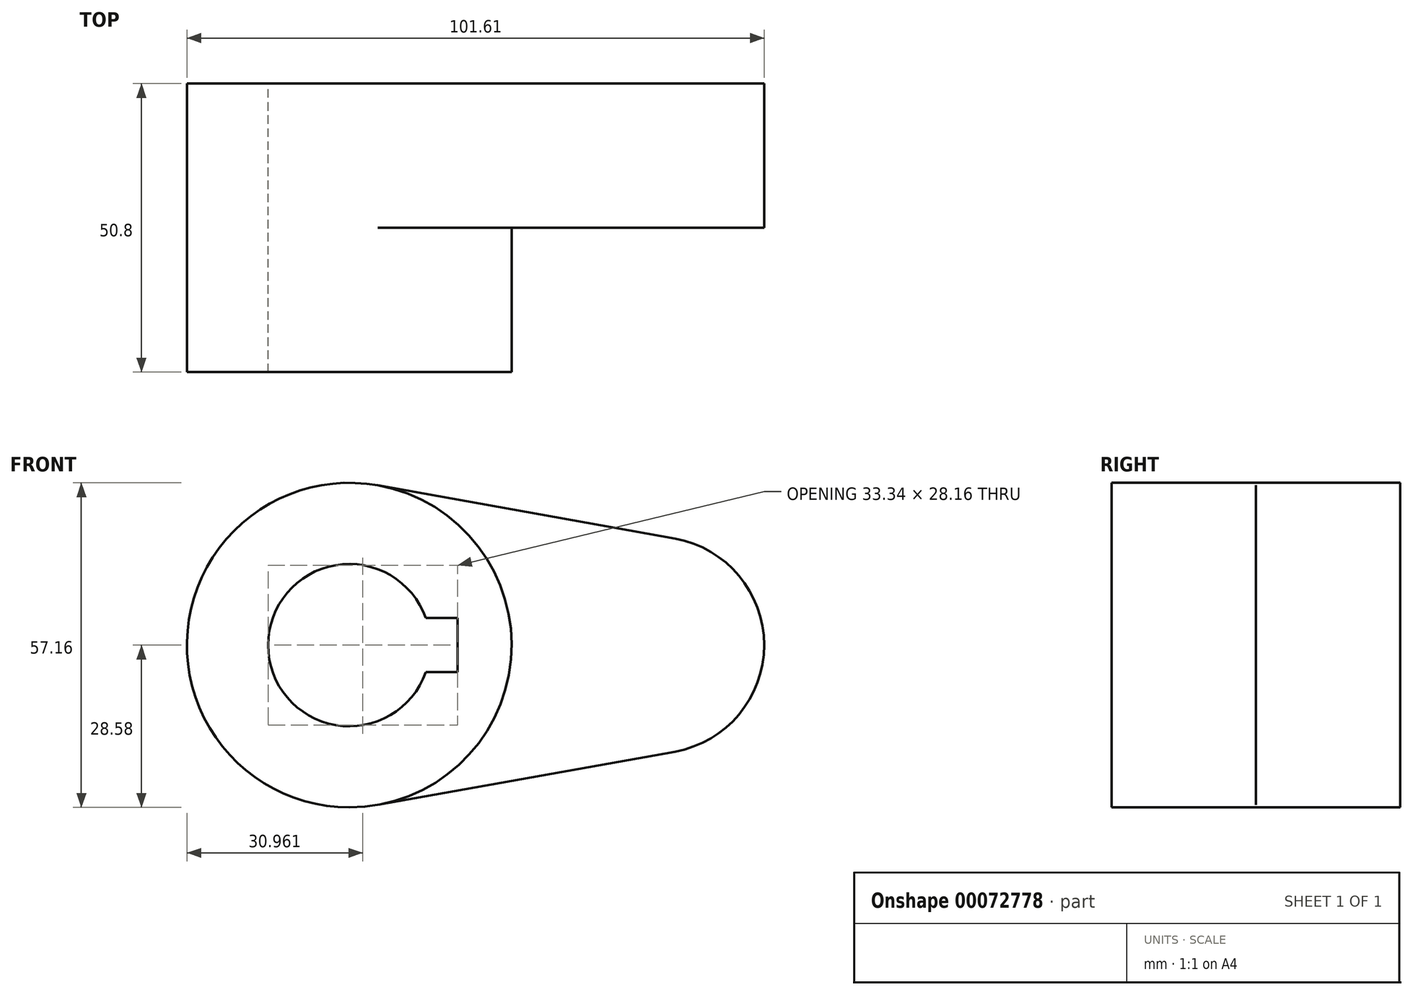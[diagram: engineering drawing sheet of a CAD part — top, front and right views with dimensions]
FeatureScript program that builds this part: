
annotation { "Feature Type Name" : "Feature", "Feature Type Description" : "" }
export const myFeature = defineFeature(function(context is Context, id is Id, definition is map)
    precondition{}
    {
        {
            var Q0;
            Q0=qCreatedBy(makeId("Front.planeOp"),FACE);
            var sketch = newSketch(context, id + "F0", { "sketchPlane" : qUnion([Q0])});
            skCircle(sketch, "E0", {"center": v(0, 0) * mm, "radius": 28.57 * mm});
            skCircle(sketch, "E1", {"center": v(53.97, 0) * mm, "radius": 19.05 * mm});
            skLineSegment(sketch, "E2", {"start": v(5.04, 28.13) * mm, "end": v(57.34, 18.75) * mm});
            skLineSegment(sketch, "E3", {"start": v(5.04, -28.13) * mm, "end": v(57.34, -18.75) * mm});
            skCircle(sketch, "E4", {"center": v(0, 0) * mm, "radius": 14.29 * mm});
            skCircle(sketch, "E5", {"center": v(53.97, 0) * mm, "radius": 14.29 * mm});
            skLineSegment(sketch, "E6.rect.bottom", {"start": v(-19.05, 4.76) * mm, "end": v(19.05, 4.76) * mm});
            skLineSegment(sketch, "E6.rect.top", {"start": v(-19.05, -4.76) * mm, "end": v(19.05, -4.76) * mm});
            skLineSegment(sketch, "E6.rect.left", {"start": v(-19.05, 4.76) * mm, "end": v(-19.05, -4.76) * mm});
            skLineSegment(sketch, "E6.rect.right", {"start": v(19.05, 4.76) * mm, "end": v(19.05, -4.76) * mm});
            skSolve(sketch);
        }
        {
            var Q0;
            {var subQ11=sQuery(id+"F0.wireOp",EDGE,"E6.rect.left");Q0=makeQuery(id+"F0.imprint","IMPRINT",FACE,{"disambiguationData":[TD([[makeQuery(id+"F0.imprint","IMPRINT",EDGE,{"derivedFrom":subQ11}),-1.0]])]});}
            var Q1;
            {var subQ0=sQuery(id+"F0.wireOp",EDGE,"E2");Q1=makeQuery(id+"F0.imprint","IMPRINT",FACE,{"disambiguationData":[TD([[makeQuery(id+"F0.imprint","IMPRINT",EDGE,{"derivedFrom":subQ0}),-1.0]])]});}
            var Q2;
            Q2=makeQuery(id+"F0.imprint","IMPRINT",FACE,{"disambiguationData":[TD([[makeQuery(id+"F0.imprint","IMPRINT",EDGE,{"derivedFrom":sQuery(id+"F0.wireOp",EDGE,"E5")}),-1.0]])]});
            var Q3;
            Q3=makeQuery(id+"F0.imprint","IMPRINT",FACE,{"disambiguationData":[TD([[makeQuery(id+"F0.imprint","IMPRINT",EDGE,{"derivedFrom":sQuery(id+"F0.wireOp",EDGE,"E5")}),1.0]])]});
            var Q4;
            {var subQ5=sQuery(id+"F0.wireOp",EDGE,"E6.rect.left");Q4=makeQuery(id+"F0.imprint","IMPRINT",FACE,{"disambiguationData":[TD([[makeQuery(id+"F0.imprint","IMPRINT",EDGE,{"derivedFrom":subQ5}),1.0]])]});}
            extrude(context, id + "F1", {"entities" : qUnion([Q0, Q1, Q2, Q3, Q4]), "depth" : 25.4 * mm});
        }
        {
            var Q0;
            {var subQ11=sQuery(id+"F0.wireOp",EDGE,"E6.rect.left");Q0=makeQuery(id+"F0.imprint","IMPRINT",FACE,{"disambiguationData":[TD([[makeQuery(id+"F0.imprint","IMPRINT",EDGE,{"derivedFrom":subQ11}),-1.0]])]});}
            var Q1;
            {var subQ5=sQuery(id+"F0.wireOp",EDGE,"E6.rect.left");Q1=makeQuery(id+"F0.imprint","IMPRINT",FACE,{"disambiguationData":[TD([[makeQuery(id+"F0.imprint","IMPRINT",EDGE,{"derivedFrom":subQ5}),1.0]])]});}
            extrude(context, id + "F2", {"entities" : qUnion([Q0, Q1]), "operationType" : NewBodyOperationType.ADD, "depth" : 50.8 * mm});
        }
    });
